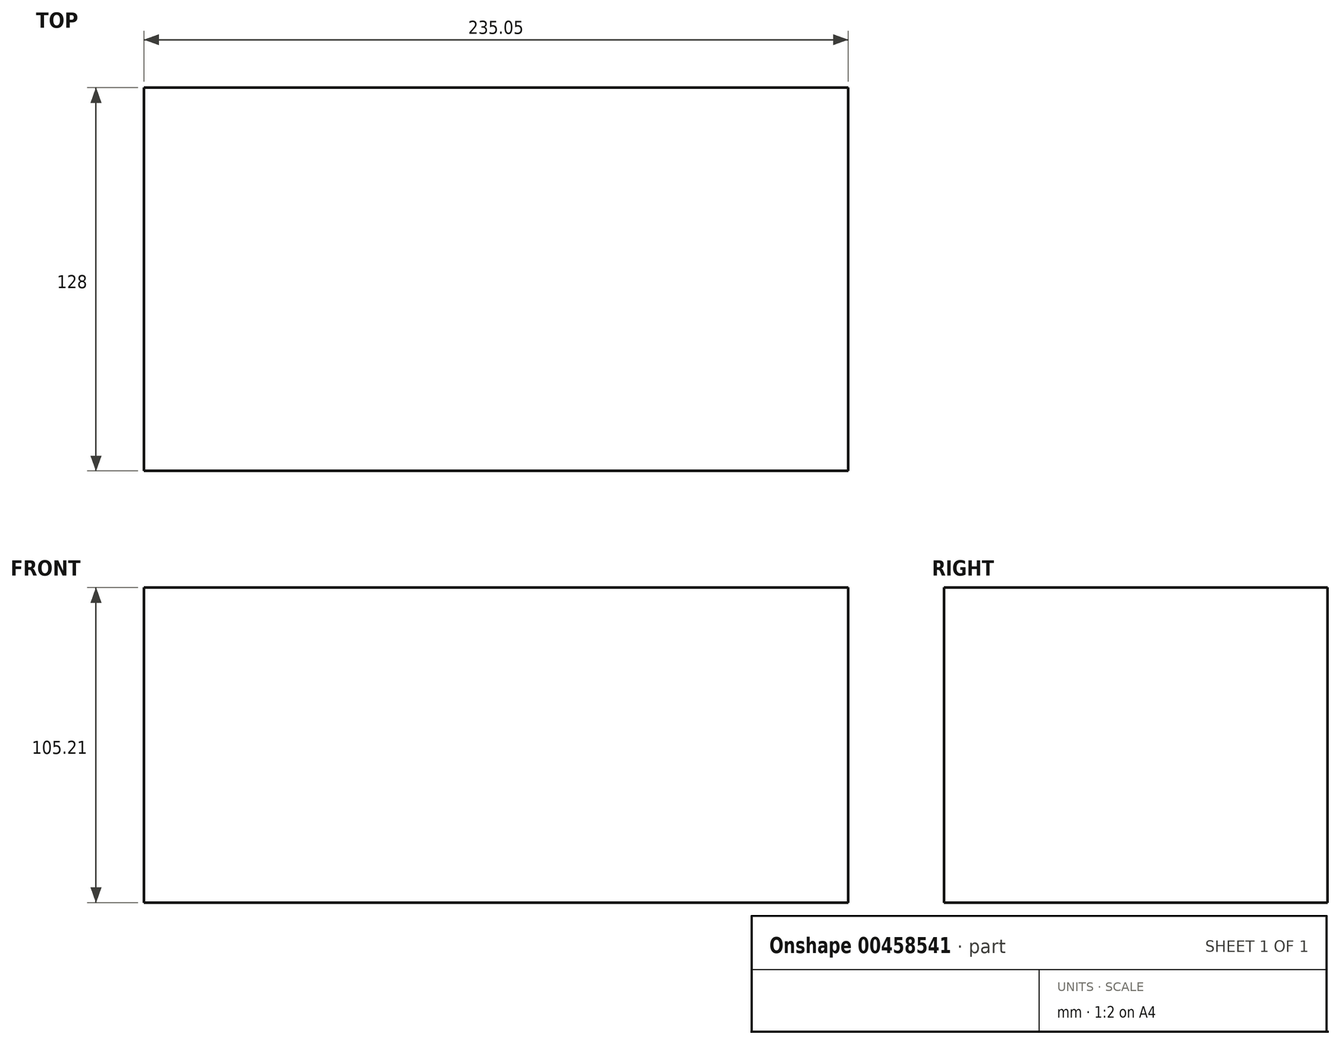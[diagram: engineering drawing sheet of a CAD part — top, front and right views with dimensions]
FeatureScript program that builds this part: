
annotation { "Feature Type Name" : "Feature", "Feature Type Description" : "" }
export const myFeature = defineFeature(function(context is Context, id is Id, definition is map)
    precondition{}
    {
        {
            var Q0;
            Q0=qCreatedBy(makeId("Front.planeOp"),FACE);
            var sketch = newSketch(context, id + "F0", { "sketchPlane" : qUnion([Q0])});
            skLineSegment(sketch, "E0.bottom", {"start": v(-111.78, 41.38) * mm, "end": v(123.27, 41.38) * mm});
            skLineSegment(sketch, "E0.top", {"start": v(-111.78, -63.83) * mm, "end": v(123.27, -63.83) * mm});
            skLineSegment(sketch, "E0.left", {"start": v(-111.78, 41.38) * mm, "end": v(-111.78, -63.83) * mm});
            skLineSegment(sketch, "E0.right", {"start": v(123.27, 41.38) * mm, "end": v(123.27, -63.83) * mm});
            skSolve(sketch);
        }
        {
            var Q0;
            Q0=makeQuery(id+"F0.imprint","IMPRINT",FACE,{"disambiguationData":[TD([[makeQuery(id+"F0.imprint","IMPRINT",EDGE,{"derivedFrom":sQuery(id+"F0.wireOp",EDGE,"E0.bottom")}),-1.0]])]});
            var sketch = newSketch(context, id + "F1", { "sketchPlane" : qUnion([Q0])});
            skCircle(sketch, "E1", {"center": v(-95.41, 22.08) * mm, "radius": 12.97 * mm});
            skCircle(sketch, "E2", {"center": v(3.13, -9.37) * mm, "radius": 20.6 * mm});
            skCircle(sketch, "E3", {"center": v(70.7, 27.2) * mm, "radius": 11.72 * mm});
            skCircle(sketch, "E4", {"center": v(83.92, -42.46) * mm, "radius": 15.02 * mm});
            skSolve(sketch);
        }
        {
            var Q0;
            Q0=makeQuery(id+"F0.imprint","IMPRINT",FACE,{"disambiguationData":[TD([[makeQuery(id+"F0.imprint","IMPRINT",EDGE,{"derivedFrom":sQuery(id+"F0.wireOp",EDGE,"E0.bottom")}),-1.0]])]});
            var Q1;
            Q1=makeQuery(id+"F1.imprint","IMPRINT",FACE,{"disambiguationData":[TD([[makeQuery(id+"F1.imprint","IMPRINT",EDGE,{"derivedFrom":sQuery(id+"F1.wireOp",EDGE,"E1")}),1.0]])]});
            var Q2;
            Q2=makeQuery(id+"F1.imprint","IMPRINT",FACE,{"disambiguationData":[TD([[makeQuery(id+"F1.imprint","IMPRINT",EDGE,{"derivedFrom":sQuery(id+"F1.wireOp",EDGE,"E2")}),1.0]])]});
            var Q3;
            Q3=makeQuery(id+"F1.imprint","IMPRINT",FACE,{"disambiguationData":[TD([[makeQuery(id+"F1.imprint","IMPRINT",EDGE,{"derivedFrom":sQuery(id+"F1.wireOp",EDGE,"E3")}),1.0]])]});
            var Q4;
            Q4=makeQuery(id+"F1.imprint","IMPRINT",FACE,{"disambiguationData":[TD([[makeQuery(id+"F1.imprint","IMPRINT",EDGE,{"derivedFrom":sQuery(id+"F1.wireOp",EDGE,"E4")}),1.0]])]});
            var Q5;
            Q5=makeQuery(id+"F1.imprint","IMPRINT",FACE,{"disambiguationData":[TD([[makeQuery(id+"F1.imprint","IMPRINT",EDGE,{"derivedFrom":sQuery(id+"F1.wireOp",EDGE,"E1")}),-1.0]])]});
            extrude(context, id + "F2", {"entities" : qUnion([Q0, Q1, Q2, Q3, Q4, Q5]), "depth" : 128 * mm});
        }
    });
